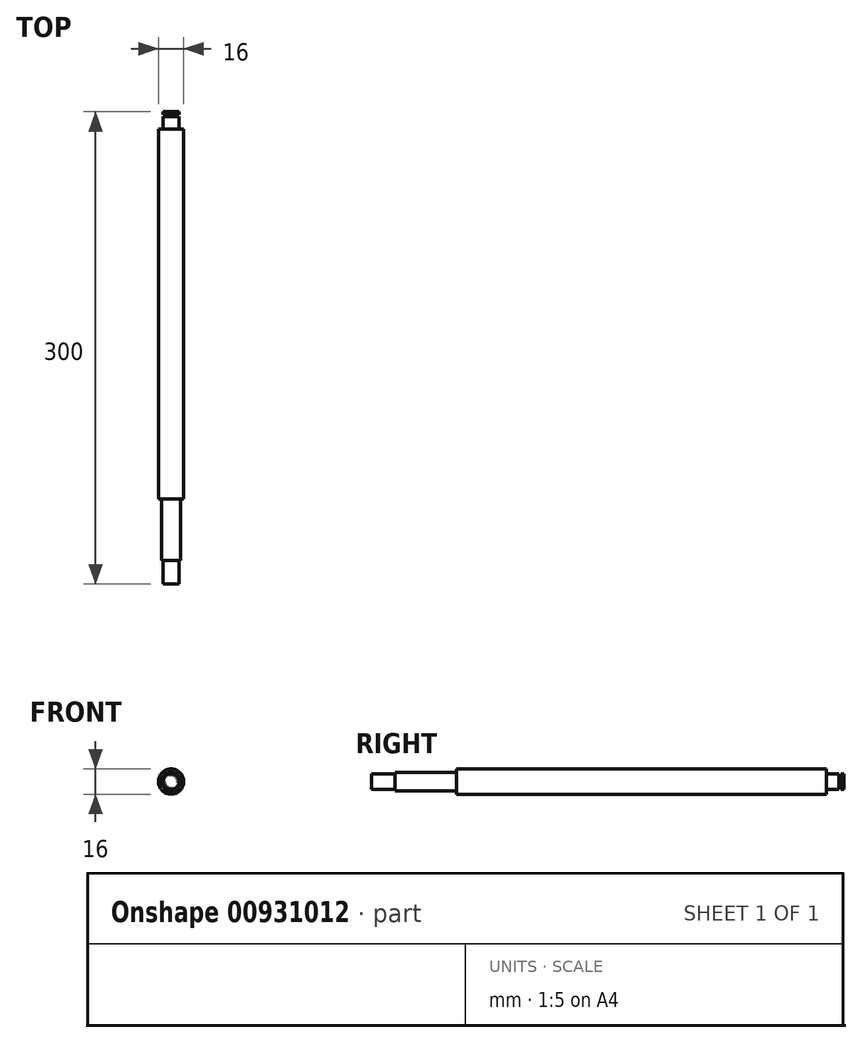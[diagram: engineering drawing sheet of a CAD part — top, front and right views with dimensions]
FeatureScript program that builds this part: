
annotation { "Feature Type Name" : "Feature", "Feature Type Description" : "" }
export const myFeature = defineFeature(function(context is Context, id is Id, definition is map)
    precondition{}
    {
        {
            var Q0;
            Q0=qCreatedBy(makeId("Front.planeOp"),FACE);
            var sketch = newSketch(context, id + "F0", { "sketchPlane" : qUnion([Q0])});
            skCircle(sketch, "E0", {"center": v(0, 0) * mm, "radius": 8 * mm});
            skSolve(sketch);
        }
        {
            var Q0;
            Q0=qSketchRegion(id+"F0",true);
            extrude(context, id + "F1", {"entities" : qUnion([Q0]), "depth" : 300 * mm, "offsetDistance" : 25 * mm});
        }
        {
            var Q0;
            Q0=qCreatedBy(makeId("Right.planeOp"),FACE);
            var sketch = newSketch(context, id + "F2", { "sketchPlane" : qUnion([Q0])});
            skLineSegment(sketch, "E1.top", {"start": v(-300, 20) * mm, "end": v(-246, 20) * mm});
            skLineSegment(sketch, "E1.left", {"start": v(-300, 0) * mm, "end": v(-300, 20) * mm, "construction": true});
            skLineSegment(sketch, "E1.right", {"start": v(-246, 6) * mm, "end": v(-246, 20) * mm});
            skLineSegment(sketch, "E2.top", {"start": v(-300, 5) * mm, "end": v(-285, 5) * mm});
            skLineSegment(sketch, "E2.left", {"start": v(-300, 0) * mm, "end": v(-300, 5) * mm, "construction": true});
            skLineSegment(sketch, "E3.top", {"start": v(-285, 6) * mm, "end": v(-246, 6) * mm});
            skLineSegment(sketch, "E3.left", {"start": v(-285, 5) * mm, "end": v(-285, 6) * mm});
            skLineSegment(sketch, "E4", {"start": v(-300, 20) * mm, "end": v(-300, 5) * mm});
            skLineSegment(sketch, "E5.top", {"start": v(0, 10) * mm, "end": v(-11, 10) * mm});
            skLineSegment(sketch, "E5.left", {"start": v(0, 5) * mm, "end": v(0, 10) * mm});
            skLineSegment(sketch, "E5.right", {"start": v(-11, 5) * mm, "end": v(-11, 10) * mm});
            skLineSegment(sketch, "E6.top", {"start": v(-3, 3.8) * mm, "end": v(-1.85, 3.8) * mm});
            skLineSegment(sketch, "E6.left", {"start": v(-3, 5) * mm, "end": v(-3, 3.8) * mm});
            skLineSegment(sketch, "E6.right", {"start": v(-1.85, 5) * mm, "end": v(-1.85, 3.8) * mm});
            skLineSegment(sketch, "E7.trimOffspring", {"start": v(-3, 5) * mm, "end": v(-11, 5) * mm});
            skLineSegment(sketch, "E8", {"start": v(-1.85, 5) * mm, "end": v(0, 5) * mm});
            skSolve(sketch);
        }
        {
            var Q0;
            Q0=qCreatedBy(makeId("Top.planeOp"),FACE);
            var sketch = newSketch(context, id + "F3", { "sketchPlane" : qUnion([Q0])});
            skLineSegment(sketch, "E9", {"start": v(0, 0) * mm, "end": v(0, -400) * mm, "construction": true});
            skSolve(sketch);
        }
        {
            var Q0;
            Q0=qSketchRegion(id+"F2",true);
            var Q1;
            Q1=sQuery(id+"F3.wireOp",EDGE,"E9");
            revolve(context, id + "F4", {"operationType" : NewBodyOperationType.REMOVE, "surfaceOperationType" : NewSurfaceOperationType.NEW, "entities" : qUnion([Q0]), "axis" : qUnion([Q1]), "revolveType" : RevolveType.FULL, "oppositeDirection" : true});
        }
    });
